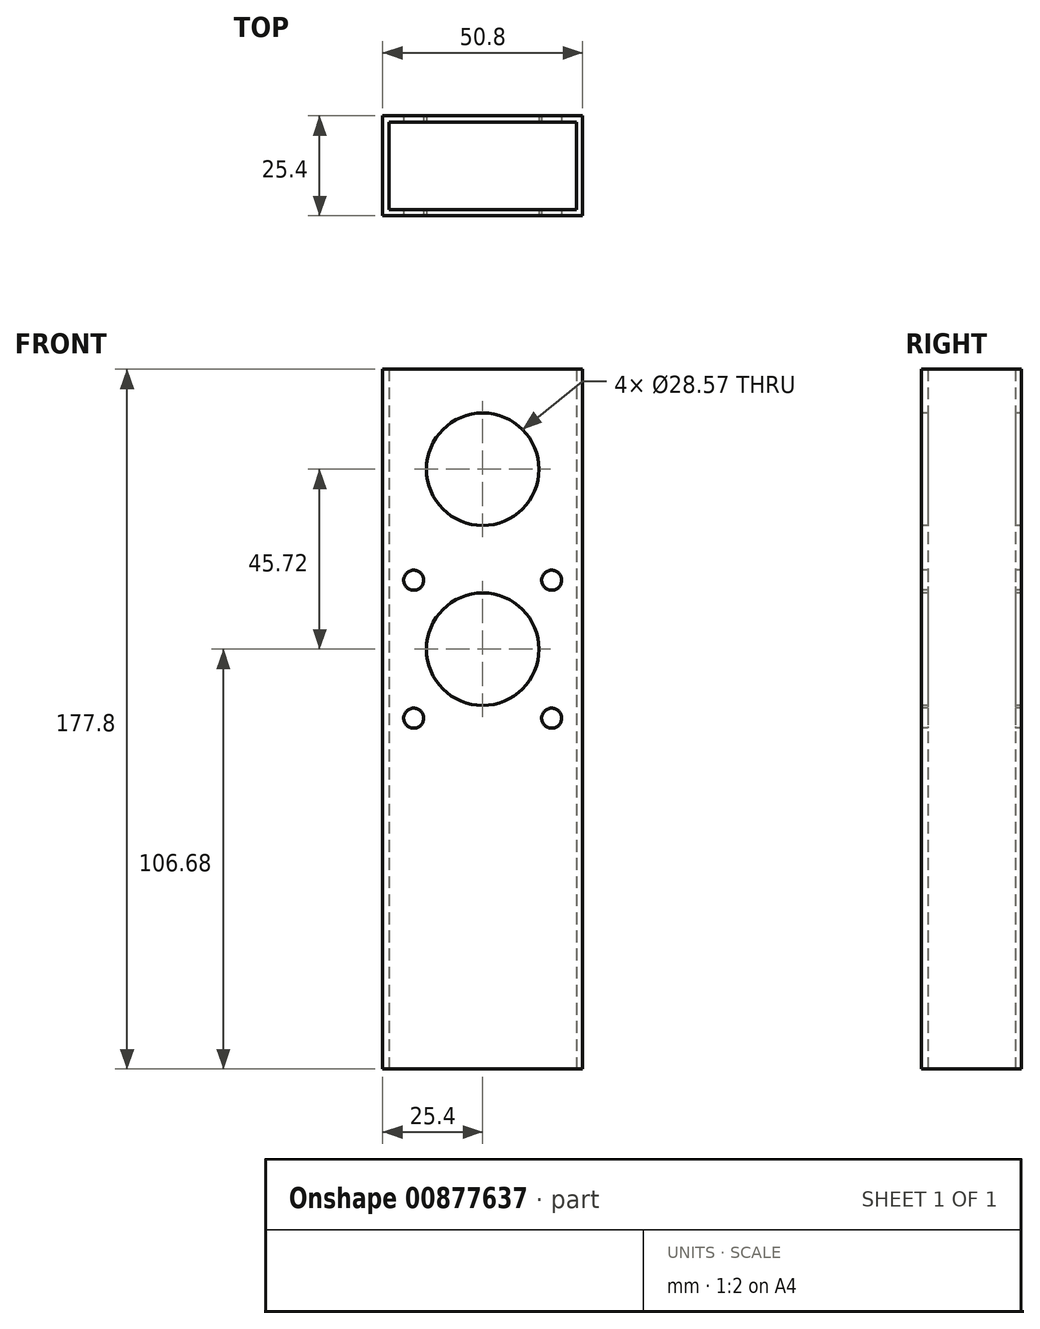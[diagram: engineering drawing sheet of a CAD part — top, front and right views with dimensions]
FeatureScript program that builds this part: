
annotation { "Feature Type Name" : "Feature", "Feature Type Description" : "" }
export const myFeature = defineFeature(function(context is Context, id is Id, definition is map)
    precondition{}
    {
        {
            var Q0;
            Q0=qCreatedBy(makeId("Top.planeOp"),FACE);
            var sketch = newSketch(context, id + "F0", { "sketchPlane" : qUnion([Q0])});
            skLineSegment(sketch, "E0.bottom", {"start": v(-25.4, 12.7) * mm, "end": v(25.4, 12.7) * mm});
            skLineSegment(sketch, "E0.top", {"start": v(-25.4, -12.7) * mm, "end": v(25.4, -12.7) * mm});
            skLineSegment(sketch, "E0.left", {"start": v(-25.4, 12.7) * mm, "end": v(-25.4, -12.7) * mm});
            skLineSegment(sketch, "E0.right", {"start": v(25.4, 12.7) * mm, "end": v(25.4, -12.7) * mm});
            skPoint(sketch, "E0.middle", {"position": v(0, 0) * mm});
            skLineSegment(sketch, "E1.bottom", {"start": v(-23.81, 11.11) * mm, "end": v(23.81, 11.11) * mm});
            skLineSegment(sketch, "E1.top", {"start": v(-23.81, -11.11) * mm, "end": v(23.81, -11.11) * mm});
            skLineSegment(sketch, "E1.left", {"start": v(-23.81, 11.11) * mm, "end": v(-23.81, -11.11) * mm});
            skLineSegment(sketch, "E1.right", {"start": v(23.81, 11.11) * mm, "end": v(23.81, -11.11) * mm});
            skSolve(sketch);
        }
        {
            var Q0;
            Q0=makeQuery(id+"F0.imprint","IMPRINT",FACE,{"disambiguationData":[TD([[makeQuery(id+"F0.imprint","IMPRINT",EDGE,{"derivedFrom":sQuery(id+"F0.wireOp",EDGE,"E0.bottom")}),-1.0]])]});
            extrude(context, id + "F1", {"entities" : qUnion([Q0]), "depth" : 177.8 * mm, "offsetDistance" : 25.4 * mm});
        }
        {
            var Q0;
            Q0=makeQuery(id+"F1.opExtrude","SWEPT_FACE",FACE,{"disambiguationData":[OSD([sQuery(id+"F0.wireOp",EDGE,"E0.top")])]});
            var sketch = newSketch(context, id + "F2", { "sketchPlane" : qUnion([Q0])});
            skCircle(sketch, "E2", {"center": v(0, 152.4) * mm, "radius": 34.3 * mm, "construction": true});
            skCircle(sketch, "E3", {"center": v(0, 106.68) * mm, "radius": 11.43 * mm, "construction": true});
            skCircle(sketch, "E4", {"center": v(0, 152.4) * mm, "radius": 14.29 * mm});
            skLineSegment(sketch, "E5.bottom", {"start": v(17.53, 124.2) * mm, "end": v(-17.53, 124.2) * mm, "construction": true});
            skLineSegment(sketch, "E5.top", {"start": v(17.53, 89.15) * mm, "end": v(-17.53, 89.15) * mm, "construction": true});
            skLineSegment(sketch, "E5.left", {"start": v(17.53, 124.2) * mm, "end": v(17.53, 89.15) * mm, "construction": true});
            skLineSegment(sketch, "E5.right", {"start": v(-17.53, 124.2) * mm, "end": v(-17.53, 89.15) * mm, "construction": true});
            skCircle(sketch, "E6", {"center": v(-17.53, 124.2) * mm, "radius": 2.55 * mm});
            skCircle(sketch, "E7", {"center": v(17.53, 124.2) * mm, "radius": 2.55 * mm});
            skCircle(sketch, "E8", {"center": v(17.53, 89.15) * mm, "radius": 2.55 * mm});
            skCircle(sketch, "E9", {"center": v(-17.53, 89.15) * mm, "radius": 2.55 * mm});
            skCircle(sketch, "E10", {"center": v(0, 106.68) * mm, "radius": 14.29 * mm});
            skSolve(sketch);
        }
        {
            var Q0;
            Q0 = qSketchRegion(id + "F2", true);
            extrude(context, id + "F3", {"entities" : qUnion([Q0]), "operationType" : NewBodyOperationType.REMOVE, "oppositeDirection" : true, "depth" : 25.4 * mm, "offsetDistance" : 25.4 * mm});
        }
    });
